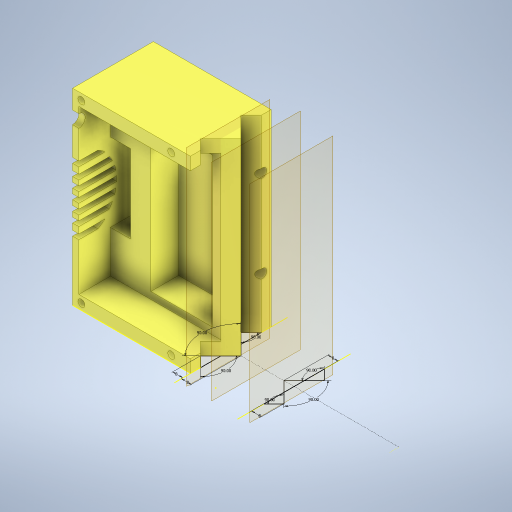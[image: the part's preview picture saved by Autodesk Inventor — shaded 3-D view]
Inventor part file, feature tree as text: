
AUTODESK INVENTOR PART (.ipt)
format: ipt  version: 2023 (Build 270158030, 158C)  size: 753,664 bytes
history: native  units: mm
features: sketch x19, extrude x18, projected_geometry x7, hole x5, mirror x2, plane x2, split x1
ambient origin geometry x8: Origin, YZ Plane, XZ Plane, XY Plane, X Axis, Y Axis, Z Axis, Center Point
bodies: Solid1 (feature_tree)
feature tree (54):
  extrude  "MainInnerBodyExtrusion"  Depth=149.0mm
  extrude  "HoleForCamerabase"  Depth=50.0mm
  extrude  "HoleForFan"  Depth=54.0mm
  extrude  "HoleForPi"  TaperAngle=0.0deg  [1 undecoded]
  extrude  "HoleForPoeAdapter"  Depth=62.0mm
  extrude  "HoleForThermister"  Depth=47.0mm
  extrude  "HoleForSensor"  Depth=32.0mm
  extrude  "SlotsForRearFan"  Depth=47.0mm
  extrude  "VentForCamera"  Depth=16.0mm
  extrude  "HoleForLens"  Depth=118.0mm
  sketch  "Sketch23"  dims[d26=49.0mm d27=118.0mm]
  hole  "Hole for 6-32 Insert"  [1 undecoded]
  hole  "Screw hole for 6-32 screw"  [1 undecoded]
  hole  "Side hole for 1-4 20 insert"  [1 undecoded]
  mirror  "Mirror for side insert"
  extrude  "Extrusion18"  Depth=17.0mm
  extrude  "HoleForPowerWire"  TaperAngle=0.0deg  [1 undecoded]
  extrude  "Extrusion22"  Depth=2.0mm
  extrude  "Extrusion23"  Depth=4.0mm
  extrude  "ExtrusionForBottom"  Depth=4.0mm
  hole  "1-4 holesToBoltFixture"  [1 undecoded]
  plane  "Work Plane1"
  plane  "Work Plane2"
  mirror  "Mirror4"
  extrude  "CutOutForFilter"  Depth=22.0mm
  hole  "Hole13"  [1 undecoded]
  split  "Split5"
  sketch  "Sketch46"  dims[d73=4.0mm d75=4.0mm]
  extrude  "Extrusion31"  Depth=149.0mm
  extrude  "Extrusion32"  Depth=10.0mm
  sketch  "Sketch1"  dims[d0=222.7mm d1=149.0mm]
  sketch  "Sketch3"  dims[d2=50.0mm d3=0.0mm d5=15.7mm]
  sketch  "Sketch4"  dims[d6=54.0mm d7=59.0mm]
  sketch  "Sketch6"  dims[d8=47.0mm d9=0.0mm]
  sketch  "Sketch7"  dims[d13=16.0mm d14=62.0mm]
  sketch  "Sketch11"  dims[d15=3.0mm d16=47.0mm]
  sketch  "Sketch15"  dims[d17=0.0mm d20=32.0mm]
  sketch  "Sketch16"  dims[d21=129.0mm d22=47.0mm]
  sketch  "Sketch18"  dims[d23=0.0mm d25=16.0mm]
  sketch  "Sketch24"  dims[d28=47.0mm d29=0.0mm]
  sketch  "Sketch25"  dims[d36=69.0mm d37=28.0mm]
  projected_geometry  "Projected Loop1"
  sketch  "Sketch26"  dims[d38=47.0mm d39=0.0mm]
  sketch  "Sketch37"  dims[d42=50.0mm d43=17.0mm]
  projected_geometry  "Projected Loop3"
  projected_geometry  "Projected Loop4"
  sketch  "Sketch39"  dims[d46=31.5mm d47=0.0mm]
  projected_geometry  "Projected Loop5"
  sketch  "Sketch40"  dims[d67=60.0mm d69=2.0mm]
  sketch  "Sketch43"  dims[d71=4.0mm d72=4.0mm]
  projected_geometry  "Projected Loop8"
  projected_geometry  "Projected Loop11"
  sketch  "Sketch47"  dims[d76=10.0mm d77=0.0mm d78=15.5mm d79=22.0mm d85=3.0mm d86=3.0mm d87=10.0mm d88=16.0mm d89=1.5mm d90=3.0mm d91=3.0mm d92=3.0mm d93=0.0mm d94=0.0mm d95=15.0mm d97=16.0mm d98=10.0mm d99=0.0mm d106=5.0mm d108=5.0mm d109=4.7mm d110=6.0mm d111=5.54mm d112=5.55mm d113=90.0deg d114=7.2mm d115=20.594885mm d116=3.797mm d117=6.0mm d118=12.7mm d119=2.362mm d120=90.0deg d121=15.0mm d122=20.594885mm d130=7.666mm d131=6.0mm d132=8.406mm d133=7.41mm d134=90.0deg d135=9.53mm d136=20.594885mm d137=24.0mm d138=10.0mm d139=3.0mm d140=25.0mm d141=0.0mm d142=30.0mm d144=10.0mm d145=0.0mm d222=76.2mm d223=76.2mm d224=76.2mm d225=76.2mm d226=25.0mm d227=111.350057mm d228=2.0mm d229=0.0mm d230=2.0mm d231=0.0mm d232=14.0mm d233=0.0mm d234=7.0mm d235=40.0mm d236=40.0mm d237=7.142mm d238=6.0mm d239=12.0mm d240=5.0mm d241=90.0deg d242=135.0mm d243=20.594885mm d246=30.0mm d247=-20.0mm d255=21.0mm d256=52.25mm d257=47.0mm d258=2.25mm d259=0.0mm d264=90.0deg d265=90.0deg d266=90.0deg d267=8.0mm d268=8.0mm d269=8.0mm d270=8.0mm d271=90.0deg d272=90.0deg d273=90.0deg d293=27.0mm d294=5.0mm d295=5.0mm d296=4.699mm d297=6.0mm d298=4.8514mm d299=5.55244mm d300=90.0deg d301=7.1374mm d302=0.0mm d303=149.0mm d304=0.0mm d305=149.0mm d306=0.0mm]
  projected_geometry  "Projected Loop12"
note: 7 required parameter values undecoded (feature->parameter linkage not recoverable at this tier; creation-order binding heuristic only, values carry confidence <= 0.55)
